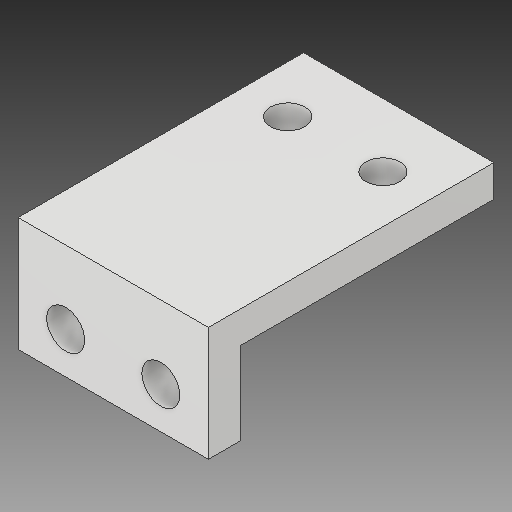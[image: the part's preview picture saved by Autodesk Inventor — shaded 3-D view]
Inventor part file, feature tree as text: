
AUTODESK INVENTOR PART (.ipt)
format: ipt  version: 2017 (Build 210142000, 142)  size: 112,640 bytes
history: native  units: in
note: dims shown in document units (in); Inventor stores cm internally (conversion verified against a paired STEP export)
features: other x3, sketch x3
ambient origin geometry x8: Origin, YZ Plane, XZ Plane, XY Plane, X Axis, Y Axis, Z Axis, Center Point
bodies: Solid1 (feature_tree)
feature tree (6):
  other  "TensionerPlate4b.ipt"
  other  "Solid1::TensionerPlate4b.ipt"
  other  "TaggingFeature1"
  sketch  "Sketch1"  dims[d0=0.3937in]
  sketch  "Sketch2"
  sketch  "Sketch3"
